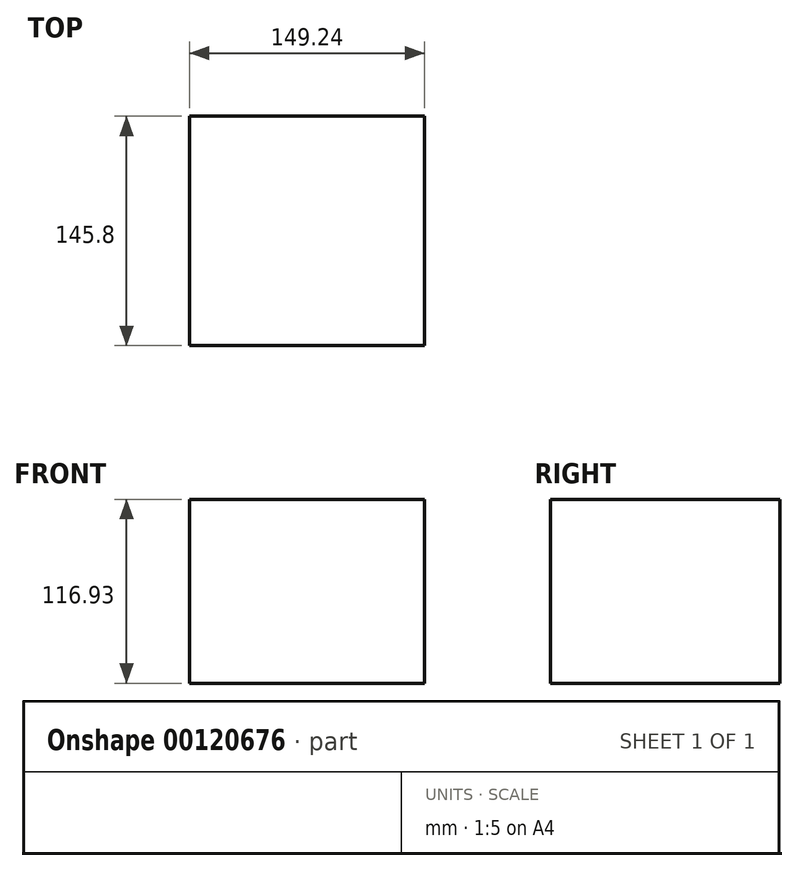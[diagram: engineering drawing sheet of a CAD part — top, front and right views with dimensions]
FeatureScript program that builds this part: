
annotation { "Feature Type Name" : "Feature", "Feature Type Description" : "" }
export const myFeature = defineFeature(function(context is Context, id is Id, definition is map)
    precondition{}
    {
        {
            var Q0;
            Q0=qCreatedBy(makeId("Top.planeOp"),FACE);
            var sketch = newSketch(context, id + "F0", { "sketchPlane" : qUnion([Q0])});
            skLineSegment(sketch, "E0", {"start": v(-75.6, 74.92) * mm, "end": v(-75.6, -74.13) * mm});
            skLineSegment(sketch, "E1", {"start": v(-75.6, -74.13) * mm, "end": v(73.64, -74.13) * mm});
            skLineSegment(sketch, "E2", {"start": v(73.64, -74.13) * mm, "end": v(73.64, 71.67) * mm});
            skLineSegment(sketch, "E3", {"start": v(73.64, 71.67) * mm, "end": v(-75.6, 71.67) * mm});
            skSolve(sketch);
        }
        {
            var Q0;
            Q0 = qSketchRegion(id + "F0", true);
            extrude(context, id + "F1", {"entities" : qUnion([Q0]), "depth" : 116.93 * mm});
        }
    });
